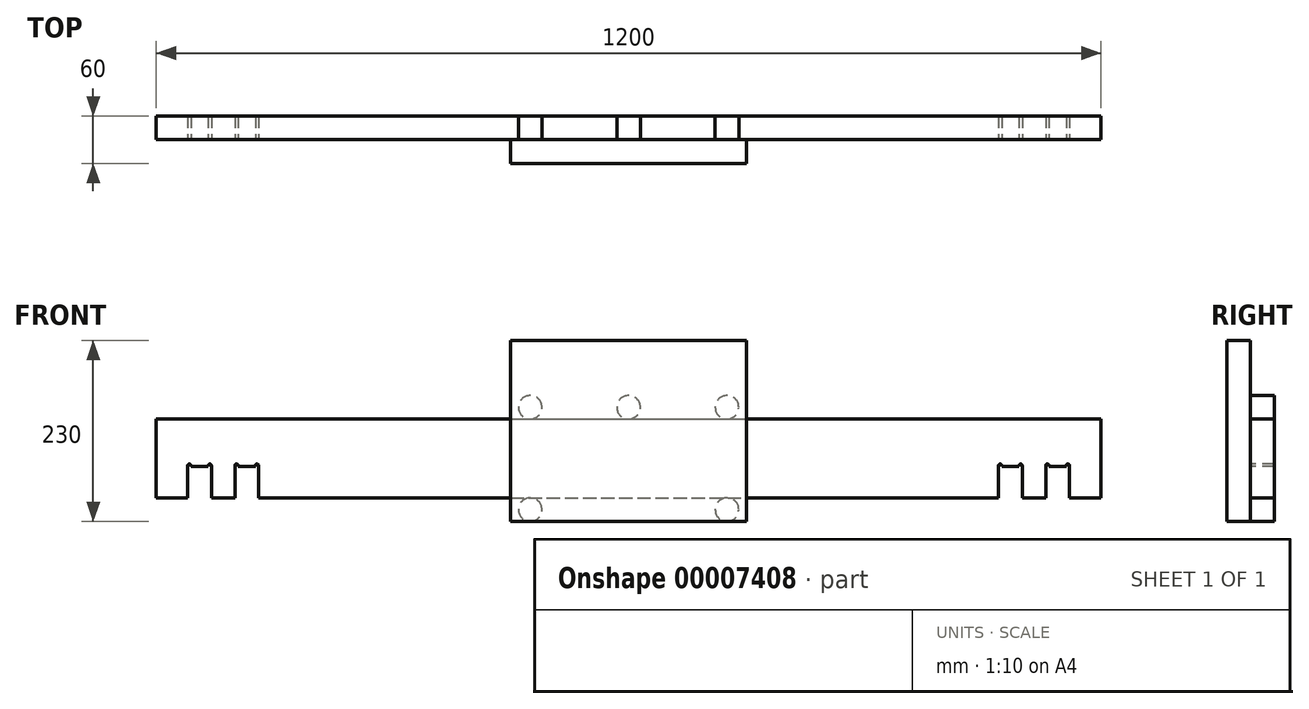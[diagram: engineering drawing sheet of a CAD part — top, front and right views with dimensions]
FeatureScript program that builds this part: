
annotation { "Feature Type Name" : "Feature", "Feature Type Description" : "" }
export const myFeature = defineFeature(function(context is Context, id is Id, definition is map)
    precondition{}
    {
        {
            var Q0;
            Q0=qCreatedBy(makeId("Front.planeOp"),FACE);
            var sketch = newSketch(context, id + "F0", { "sketchPlane" : qUnion([Q0])});
            skLineSegment(sketch, "E0.bottom", {"start": v(0, 0) * mm, "end": v(1200, 0) * mm});
            skLineSegment(sketch, "E0.top", {"start": v(0, 100) * mm, "end": v(1200, 100) * mm});
            skLineSegment(sketch, "E0.left", {"start": v(0, 0) * mm, "end": v(0, 100) * mm});
            skLineSegment(sketch, "E0.right", {"start": v(1200, 0) * mm, "end": v(1200, 100) * mm});
            skSolve(sketch);
        }
        {
            var Q0;
            Q0=makeQuery(id+"F0.imprint","IMPRINT",FACE,{"disambiguationData":[TD([[makeQuery(id+"F0.imprint","IMPRINT",EDGE,{"derivedFrom":sQuery(id+"F0.wireOp",EDGE,"E0.bottom")}),1.0]])]});
            extrude(context, id + "F1", {"entities" : qUnion([Q0]), "depth" : 30 * mm});
        }
        {
            var Q0;
            Q0=makeQuery(id+"F1.opExtrude","CAP_FACE",FACE,{"disambiguationData":[OSD([sQuery(id+"F0.wireOp",EDGE,"E0.bottom"),sQuery(id+"F0.wireOp",EDGE,"E0.top"),sQuery(id+"F0.wireOp",EDGE,"E0.left"),sQuery(id+"F0.wireOp",EDGE,"E0.right")])],"isStart":false});
            var sketch = newSketch(context, id + "F2", { "sketchPlane" : qUnion([Q0])});
            skLineSegment(sketch, "E1", {"start": v(600, 0) * mm, "end": v(600, 100) * mm, "construction": true});
            skLineSegment(sketch, "E2.bottom", {"start": v(130, 0) * mm, "end": v(100, 0) * mm});
            skLineSegment(sketch, "E2.top", {"start": v(130, 40) * mm, "end": v(100, 40) * mm});
            skLineSegment(sketch, "E2.left", {"start": v(130, 0) * mm, "end": v(130, 40) * mm});
            skLineSegment(sketch, "E2.right", {"start": v(100, 0) * mm, "end": v(100, 40) * mm});
            skLineSegment(sketch, "E3.bottom", {"start": v(1070, 0) * mm, "end": v(1100, 0) * mm});
            skLineSegment(sketch, "E3.top", {"start": v(1070, 40) * mm, "end": v(1100, 40) * mm});
            skLineSegment(sketch, "E3.left", {"start": v(1070, 0) * mm, "end": v(1070, 40) * mm});
            skLineSegment(sketch, "E3.right", {"start": v(1100, 0) * mm, "end": v(1100, 40) * mm});
            skLineSegment(sketch, "E4", {"start": v(130, 20) * mm, "end": v(600, 20) * mm, "construction": true});
            skLineSegment(sketch, "E5", {"start": v(600, 20) * mm, "end": v(1070, 20) * mm, "construction": true});
            skLineSegment(sketch, "E6.bottom", {"start": v(70, 40) * mm, "end": v(40, 40) * mm});
            skLineSegment(sketch, "E6.top", {"start": v(70, 0) * mm, "end": v(40, 0) * mm});
            skLineSegment(sketch, "E6.left", {"start": v(70, 40) * mm, "end": v(70, 0) * mm});
            skLineSegment(sketch, "E6.right", {"start": v(40, 40) * mm, "end": v(40, 0) * mm});
            skLineSegment(sketch, "E7.0.MirrorCS", {"start": v(1130, 40) * mm, "end": v(1130, 0) * mm});
            skLineSegment(sketch, "E7.1.MirrorCS", {"start": v(1160, 40) * mm, "end": v(1160, 0) * mm});
            skLineSegment(sketch, "E7.2.MirrorCS", {"start": v(1130, 40) * mm, "end": v(1160, 40) * mm});
            skLineSegment(sketch, "E7.3.MirrorCS", {"start": v(1130, 0) * mm, "end": v(1160, 0) * mm});
            skLineSegment(sketch, "E8", {"start": v(40, 40) * mm, "end": v(40, 41) * mm});
            skLineSegment(sketch, "E9", {"start": v(44, 40) * mm, "end": v(44, 41) * mm});
            skArc(sketch, "E10", {"start": v(44, 41) * mm, "mid": v(42, 43) * mm, "end": v(40, 41) * mm});
            skLineSegment(sketch, "E11", {"start": v(55, 40) * mm, "end": v(55, 0) * mm, "construction": true});
            skLineSegment(sketch, "E12", {"start": v(70, 40) * mm, "end": v(100, 40) * mm, "construction": true});
            skLineSegment(sketch, "E13", {"start": v(85, 40) * mm, "end": v(85, 0) * mm, "construction": true});
            skLineSegment(sketch, "E14.0.MirrorCS", {"start": v(70, 40) * mm, "end": v(70, 41) * mm});
            skLineSegment(sketch, "E14.1.MirrorCS", {"start": v(66, 40) * mm, "end": v(66, 41) * mm});
            skArc(sketch, "E14.2.MirrorCS", {"start": v(66, 41) * mm, "mid": v(68, 43) * mm, "end": v(70, 41) * mm});
            skLineSegment(sketch, "E15.0.MirrorCS", {"start": v(25, 40) * mm, "end": v(25, 0) * mm, "construction": true});
            skLineSegment(sketch, "E16.0.MirrorCS", {"start": v(130, 40) * mm, "end": v(130, 41) * mm});
            skLineSegment(sketch, "E16.1.MirrorCS", {"start": v(104, 40) * mm, "end": v(104, 41) * mm});
            skLineSegment(sketch, "E16.2.MirrorCS", {"start": v(100, 40) * mm, "end": v(100, 41) * mm});
            skLineSegment(sketch, "E16.3.MirrorCS", {"start": v(126, 40) * mm, "end": v(126, 41) * mm});
            skLineSegment(sketch, "E16.4.MirrorCS", {"start": v(100, 40) * mm, "end": v(130, 40) * mm});
            skArc(sketch, "E16.5.MirrorCS", {"start": v(104, 41) * mm, "mid": v(102, 43) * mm, "end": v(100, 41) * mm});
            skArc(sketch, "E16.6.MirrorCS", {"start": v(126, 41) * mm, "mid": v(128, 43) * mm, "end": v(130, 41) * mm});
            skLineSegment(sketch, "E17.0.MirrorCS", {"start": v(1070, 40) * mm, "end": v(1070, 41) * mm});
            skArc(sketch, "E17.1.MirrorCS", {"start": v(1156, 41) * mm, "mid": v(1158, 43) * mm, "end": v(1160, 41) * mm});
            skLineSegment(sketch, "E17.2.MirrorCS", {"start": v(1096, 40) * mm, "end": v(1096, 41) * mm});
            skLineSegment(sketch, "E17.3.MirrorCS", {"start": v(1156, 40) * mm, "end": v(1156, 41) * mm});
            skLineSegment(sketch, "E17.4.MirrorCS", {"start": v(1130, 40) * mm, "end": v(1130, 41) * mm});
            skArc(sketch, "E17.5.MirrorCS", {"start": v(1096, 41) * mm, "mid": v(1098, 43) * mm, "end": v(1100, 41) * mm});
            skLineSegment(sketch, "E17.6.MirrorCS", {"start": v(1100, 40) * mm, "end": v(1100, 41) * mm});
            skLineSegment(sketch, "E17.7.MirrorCS", {"start": v(1160, 40) * mm, "end": v(1160, 41) * mm});
            skLineSegment(sketch, "E17.8.MirrorCS", {"start": v(1074, 40) * mm, "end": v(1074, 41) * mm});
            skArc(sketch, "E17.9.MirrorCS", {"start": v(1074, 41) * mm, "mid": v(1072, 43) * mm, "end": v(1070, 41) * mm});
            skLineSegment(sketch, "E17.10.MirrorCS", {"start": v(1100, 40) * mm, "end": v(1070, 40) * mm});
            skArc(sketch, "E17.11.MirrorCS", {"start": v(1134, 41) * mm, "mid": v(1132, 43) * mm, "end": v(1130, 41) * mm});
            skLineSegment(sketch, "E17.12.MirrorCS", {"start": v(1134, 40) * mm, "end": v(1134, 41) * mm});
            skLineSegment(sketch, "E17.14.MirrorCS", {"start": v(1130, 40) * mm, "end": v(1100, 40) * mm, "construction": true});
            skSolve(sketch);
        }
        {
            var Q0;
            Q0 = qSketchRegion(id + "F2", true);
            var Q1;
            Q1=makeQuery(id+"F1.opExtrude","CAP_FACE",FACE,{"disambiguationData":[OSD([sQuery(id+"F0.wireOp",EDGE,"E0.bottom"),sQuery(id+"F0.wireOp",EDGE,"E0.top"),sQuery(id+"F0.wireOp",EDGE,"E0.left"),sQuery(id+"F0.wireOp",EDGE,"E0.right")])],"isStart":true});
            extrude(context, id + "F3", {"entities" : qUnion([Q0]), "operationType" : NewBodyOperationType.REMOVE, "endBound" : BoundingType.UP_TO_SURFACE, "oppositeDirection" : true, "endBoundEntityFace" : qUnion([Q1]), "depth" : 25 * mm});
        }
        {
            var Q0;
            Q0=makeQuery(id+"F1.opExtrude","CAP_FACE",FACE,{"disambiguationData":[OSD([sQuery(id+"F0.wireOp",EDGE,"E0.bottom"),sQuery(id+"F0.wireOp",EDGE,"E0.top"),sQuery(id+"F0.wireOp",EDGE,"E0.left"),sQuery(id+"F0.wireOp",EDGE,"E0.right")])],"isStart":false});
            var sketch = newSketch(context, id + "F4", { "sketchPlane" : qUnion([Q0])});
            skLineSegment(sketch, "E18.bottom", {"start": v(450, -30) * mm, "end": v(750, -30) * mm});
            skLineSegment(sketch, "E18.top", {"start": v(450, 200) * mm, "end": v(750, 200) * mm});
            skLineSegment(sketch, "E18.left", {"start": v(450, -30) * mm, "end": v(450, 200) * mm});
            skLineSegment(sketch, "E18.right", {"start": v(750, -30) * mm, "end": v(750, 200) * mm});
            skLineSegment(sketch, "E19", {"start": v(600, 100) * mm, "end": v(600, 200) * mm, "construction": true});
            skSolve(sketch);
        }
        {
            var Q0;
            Q0 = qSketchRegion(id + "F4", true);
            extrude(context, id + "F5", {"entities" : qUnion([Q0]), "depth" : 30 * mm});
        }
        {
            var Q0;
            Q0=makeQuery(id+"F5.opExtrude","CAP_FACE",FACE,{"disambiguationData":[OSD([sQuery(id+"F4.wireOp",EDGE,"E18.bottom"),sQuery(id+"F4.wireOp",EDGE,"E18.top"),sQuery(id+"F4.wireOp",EDGE,"E18.left"),sQuery(id+"F4.wireOp",EDGE,"E18.right")])],"isStart":true});
            var sketch = newSketch(context, id + "F6", { "sketchPlane" : qUnion([Q0])});
            skLineSegment(sketch, "E20", {"start": v(-600, 200) * mm, "end": v(-600, -30) * mm, "construction": true});
            skCircle(sketch, "E21", {"center": v(-725, 115) * mm, "radius": 15 * mm});
            skCircle(sketch, "E22", {"center": v(-600, 115) * mm, "radius": 15 * mm});
            skCircle(sketch, "E23", {"center": v(-475, 115) * mm, "radius": 15 * mm});
            skCircle(sketch, "E24", {"center": v(-725, -15) * mm, "radius": 15 * mm});
            skCircle(sketch, "E25", {"center": v(-475, -15) * mm, "radius": 15 * mm});
            skLineSegment(sketch, "E26", {"start": v(-725, 115) * mm, "end": v(-475, 115) * mm, "construction": true});
            skLineSegment(sketch, "E27", {"start": v(-725, 115) * mm, "end": v(-725, -15) * mm, "construction": true});
            skLineSegment(sketch, "E28", {"start": v(-475, -15) * mm, "end": v(-725, -15) * mm, "construction": true});
            skSolve(sketch);
        }
        {
            var Q0;
            Q0=makeQuery(id+"F6.imprint","IMPRINT",FACE,{"disambiguationData":[TD([[makeQuery(id+"F6.imprint","IMPRINT",EDGE,{"derivedFrom":sQuery(id+"F6.wireOp",EDGE,"E21")}),1.0]])]});
            var Q1;
            Q1=makeQuery(id+"F6.imprint","IMPRINT",FACE,{"disambiguationData":[TD([[makeQuery(id+"F6.imprint","IMPRINT",EDGE,{"derivedFrom":sQuery(id+"F6.wireOp",EDGE,"E22")}),1.0]])]});
            var Q2;
            Q2=makeQuery(id+"F6.imprint","IMPRINT",FACE,{"disambiguationData":[TD([[makeQuery(id+"F6.imprint","IMPRINT",EDGE,{"derivedFrom":sQuery(id+"F6.wireOp",EDGE,"E23")}),1.0]])]});
            var Q3;
            Q3=makeQuery(id+"F6.imprint","IMPRINT",FACE,{"disambiguationData":[TD([[makeQuery(id+"F6.imprint","IMPRINT",EDGE,{"derivedFrom":sQuery(id+"F6.wireOp",EDGE,"E25")}),1.0]])]});
            var Q4;
            Q4=makeQuery(id+"F6.imprint","IMPRINT",FACE,{"disambiguationData":[TD([[makeQuery(id+"F6.imprint","IMPRINT",EDGE,{"derivedFrom":sQuery(id+"F6.wireOp",EDGE,"E24")}),1.0]])]});
            extrude(context, id + "F7", {"entities" : qUnion([Q0, Q1, Q2, Q3, Q4]), "depth" : 30 * mm});
        }
    });
